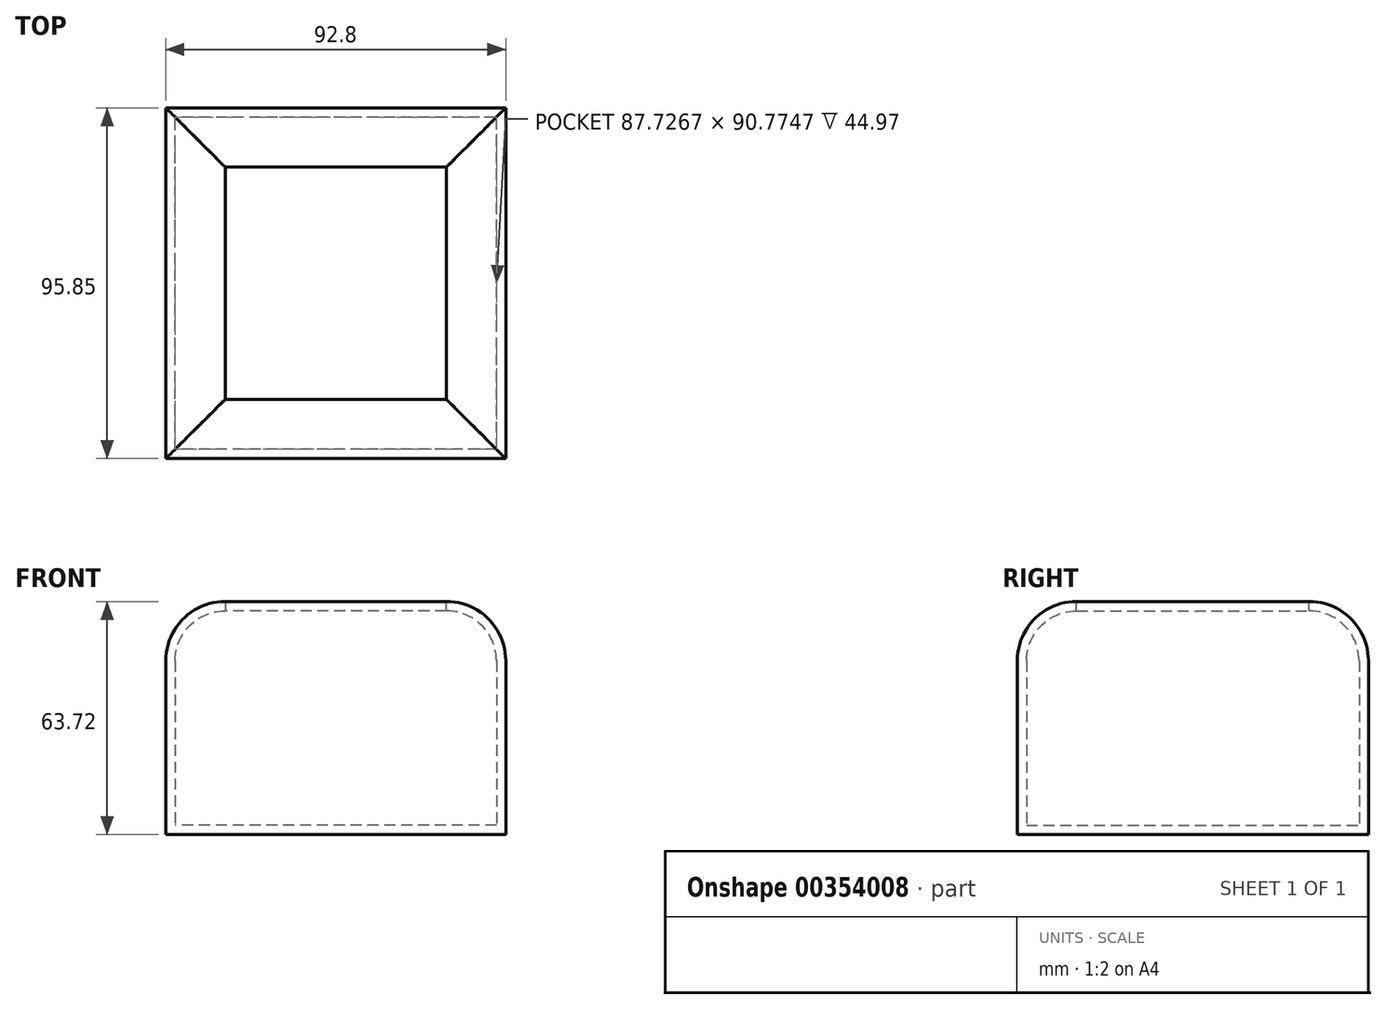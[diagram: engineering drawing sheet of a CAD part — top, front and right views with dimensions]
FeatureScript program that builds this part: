
annotation { "Feature Type Name" : "Feature", "Feature Type Description" : "" }
export const myFeature = defineFeature(function(context is Context, id is Id, definition is map)
    precondition{}
    {
        {
            var Q0;
            Q0=qCreatedBy(makeId("Top.planeOp"),FACE);
            var sketch = newSketch(context, id + "F0", { "sketchPlane" : qUnion([Q0])});
            skLineSegment(sketch, "E0.bottom", {"start": v(47.06, -50.72) * mm, "end": v(-45.74, -50.72) * mm});
            skLineSegment(sketch, "E0.top", {"start": v(47.06, 45.13) * mm, "end": v(-45.74, 45.13) * mm});
            skLineSegment(sketch, "E0.left", {"start": v(47.06, -50.72) * mm, "end": v(47.06, 45.13) * mm});
            skLineSegment(sketch, "E0.right", {"start": v(-45.74, -50.72) * mm, "end": v(-45.74, 45.13) * mm});
            skSolve(sketch);
        }
        {
            var Q0;
            Q0=makeQuery(id+"F0.imprint","IMPRINT",FACE,{"disambiguationData":[TD([[makeQuery(id+"F0.imprint","IMPRINT",EDGE,{"derivedFrom":sQuery(id+"F0.wireOp",EDGE,"E0.bottom")}),-1.0]])]});
            extrude(context, id + "F1", {"entities" : qUnion([Q0]), "depth" : 63.72 * mm});
        }
        {
            var Q0;
            Q0=makeQuery(id+"F1.opExtrude","CAP_EDGE",EDGE,{"disambiguationData":[OSD([sQuery(id+"F0.wireOp",EDGE,"E0.right")])],"isStart":false});
            var Q1;
            Q1=makeQuery(id+"F1.opExtrude","CAP_EDGE",EDGE,{"disambiguationData":[OSD([sQuery(id+"F0.wireOp",EDGE,"E0.bottom")])],"isStart":false});
            var Q2;
            Q2=makeQuery(id+"F1.opExtrude","CAP_EDGE",EDGE,{"disambiguationData":[OSD([sQuery(id+"F0.wireOp",EDGE,"E0.left")])],"isStart":false});
            var Q3;
            Q3=makeQuery(id+"F1.opExtrude","CAP_EDGE",EDGE,{"disambiguationData":[OSD([sQuery(id+"F0.wireOp",EDGE,"E0.top")])],"isStart":false});
            fillet(context, id + "F2", {"entities" : qUnion([Q0, Q1, Q2, Q3]), "radius" : 16.21 * mm, "tangentPropagation" : true, "allowEdgeOverflow" : false});
        }
        {
            var Q0;
            Q0=makeQuery(id+"F1.opExtrude","CAP_FACE",FACE,{"disambiguationData":[OSD([sQuery(id+"F0.wireOp",EDGE,"E0.bottom"),sQuery(id+"F0.wireOp",EDGE,"E0.top"),sQuery(id+"F0.wireOp",EDGE,"E0.left"),sQuery(id+"F0.wireOp",EDGE,"E0.right")])],"isStart":false});
            shell(context, id + "F3", {"entities" : qUnion([Q0]), "thickness" : 2.54 * mm});
        }
    });
